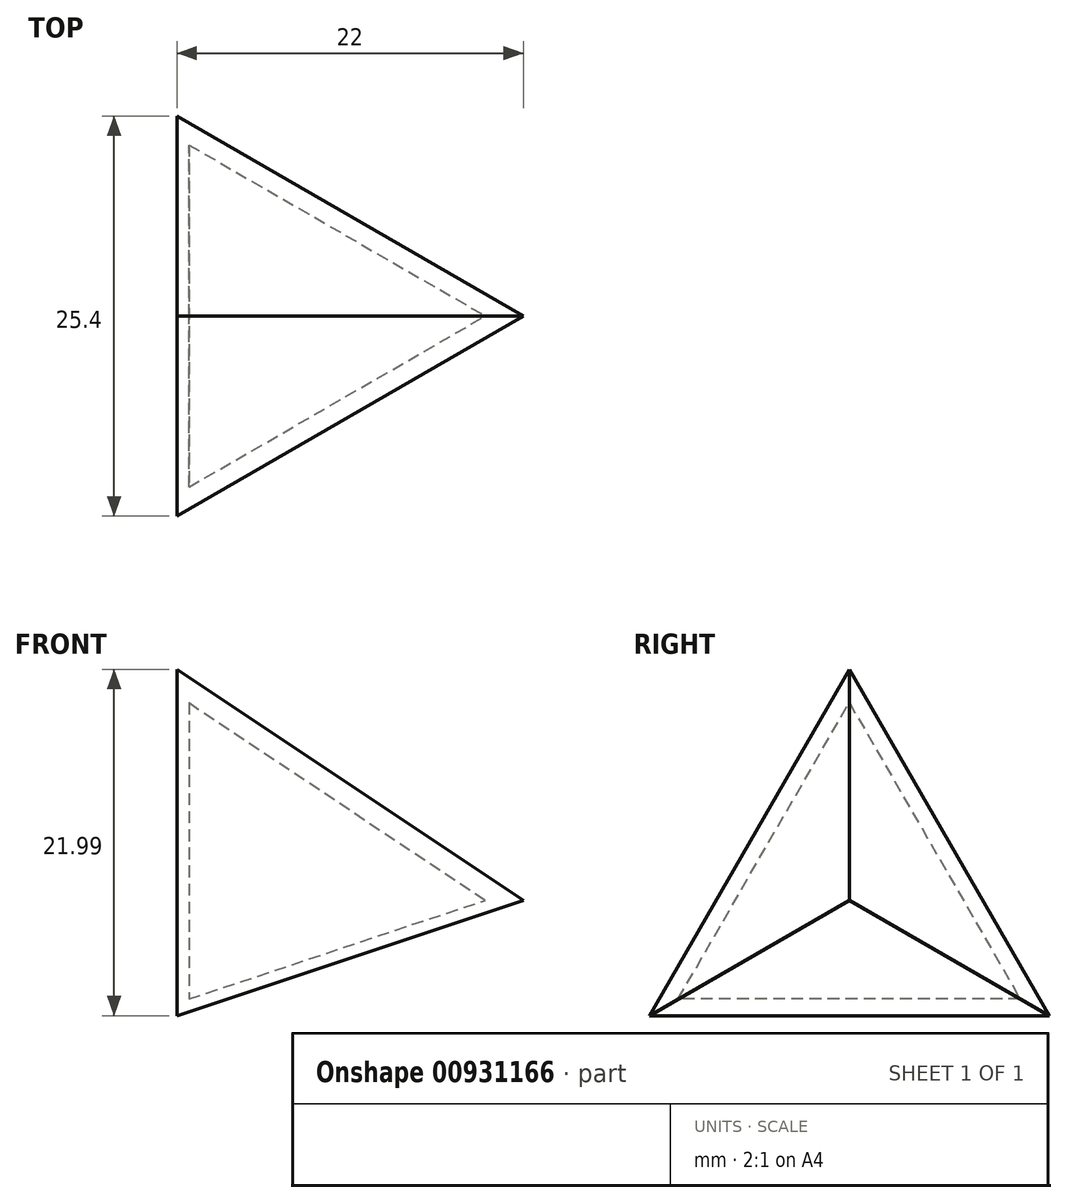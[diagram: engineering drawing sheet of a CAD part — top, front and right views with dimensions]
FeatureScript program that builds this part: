
annotation { "Feature Type Name" : "Feature", "Feature Type Description" : "" }
export const myFeature = defineFeature(function(context is Context, id is Id, definition is map)
    precondition{}
    {
        {
            var Q0;
            Q0=qCreatedBy(makeId("Right.planeOp"),FACE);
            var sketch = newSketch(context, id + "F0", { "sketchPlane" : qUnion([Q0])});
            skCircle(sketch, "E0.cCircle", {"center": v(0, 0) * mm, "radius": 7.33 * mm, "construction": true});
            skLineSegment(sketch, "E0.0", {"start": v(0, 14.66) * mm, "end": v(12.7, -7.33) * mm});
            skLineSegment(sketch, "E0.1", {"start": v(12.7, -7.33) * mm, "end": v(-12.7, -7.33) * mm});
            skLineSegment(sketch, "E0.2", {"start": v(-12.7, -7.33) * mm, "end": v(0, 14.66) * mm});
            skPoint(sketch, "E0.0.midPoint", {"position": v(6.35, 3.67) * mm});
            skSolve(sketch);
        }
        {
            var Q0;
            Q0=makeQuery(id+"F0.imprint","IMPRINT",FACE,{"disambiguationData":[TD([[makeQuery(id+"F0.imprint","IMPRINT",EDGE,{"derivedFrom":sQuery(id+"F0.wireOp",EDGE,"E0.0")}),-1.0]])]});
            cPlane(context, id + "F1", {"entities" : qUnion([Q0]), "cplaneType" : CPlaneType.OFFSET, "offset" : 22 * mm, "width" : 152.4 * mm, "height" : 152.4 * mm});
        }
        {
            var Q0;
            Q0=qCreatedBy(id+"F1.planeOp",FACE);
            var sketch = newSketch(context, id + "F2", { "sketchPlane" : qUnion([Q0])});
            skCircle(sketch, "E1.cCircle", {"center": v(0, 0) * mm, "radius": 7.23 * mm, "construction": true});
            skLineSegment(sketch, "E1.0", {"start": v(14.31, 2.07) * mm, "end": v(-5.37, -13.43) * mm});
            skLineSegment(sketch, "E1.1", {"start": v(-5.37, -13.43) * mm, "end": v(-8.94, 11.36) * mm});
            skLineSegment(sketch, "E1.2", {"start": v(-8.94, 11.36) * mm, "end": v(14.31, 2.07) * mm});
            skPoint(sketch, "E1.0.midPoint", {"position": v(4.47, -5.68) * mm});
            skSolve(sketch);
        }
        {
            var Q0;
            Q0=makeQuery(id+"F0.imprint","IMPRINT",FACE,{"disambiguationData":[TD([[makeQuery(id+"F0.imprint","IMPRINT",EDGE,{"derivedFrom":sQuery(id+"F0.wireOp",EDGE,"E0.0")}),-1.0]])]});
            var Q1;
            Q1=sQuery(id+"F2.wireOp",VERTEX,"E1.cCircle.center");
            loft(context, id + "F3", {"sheetProfilesArray" : [{ "sheetProfileEntities" : qUnion([Q0]) }, { "sheetProfileEntities" : qUnion([Q1]) }]});
        }
        {
            var Q0;
            {var subQ0=sQuery(id+"F0.wireOp",EDGE,"E0.2");var subQ1=sQuery(id+"F0.wireOp",EDGE,"E0.1");var subQ2=sQuery(id+"F0.wireOp",EDGE,"E0.0");Q0=makeQuery(id+"F3.opLoft","SWEPT_FACE",FACE,{"disambiguationData":[OSD([subQ2,subQ1,subQ0]),TDD([makeQuery(id+"F0.imprint","INTERSECT",VERTEX,{"derivedFrom":[subQ2,subQ0]}),makeQuery(id+"F0.imprint","INTERSECT",VERTEX,{"derivedFrom":[subQ1,subQ0]}),makeQuery(id+"F0.imprint","IMPRINT",EDGE,{"derivedFrom":subQ0})])]});}
            var Q1;
            Q1=makeQuery(id+"F3.opLoft","SWEPT_BODY",BODY,{"disambiguationData":[OSD([makeQuery(id+"F0.imprint","IMPRINT",FACE,{"disambiguationData":[TD([[makeQuery(id+"F0.imprint","IMPRINT",EDGE,{"derivedFrom":sQuery(id+"F0.wireOp",EDGE,"E0.0")}),-1.0]])]}),sQuery(id+"F2.wireOp",VERTEX,"E1.cCircle.center")])]});
            shell(context, id + "F4", {"isHollow" : true, "entities" : qUnion([Q0]), "parts" : qUnion([Q1]), "thickness" : 0.76 * mm});
        }
    });
